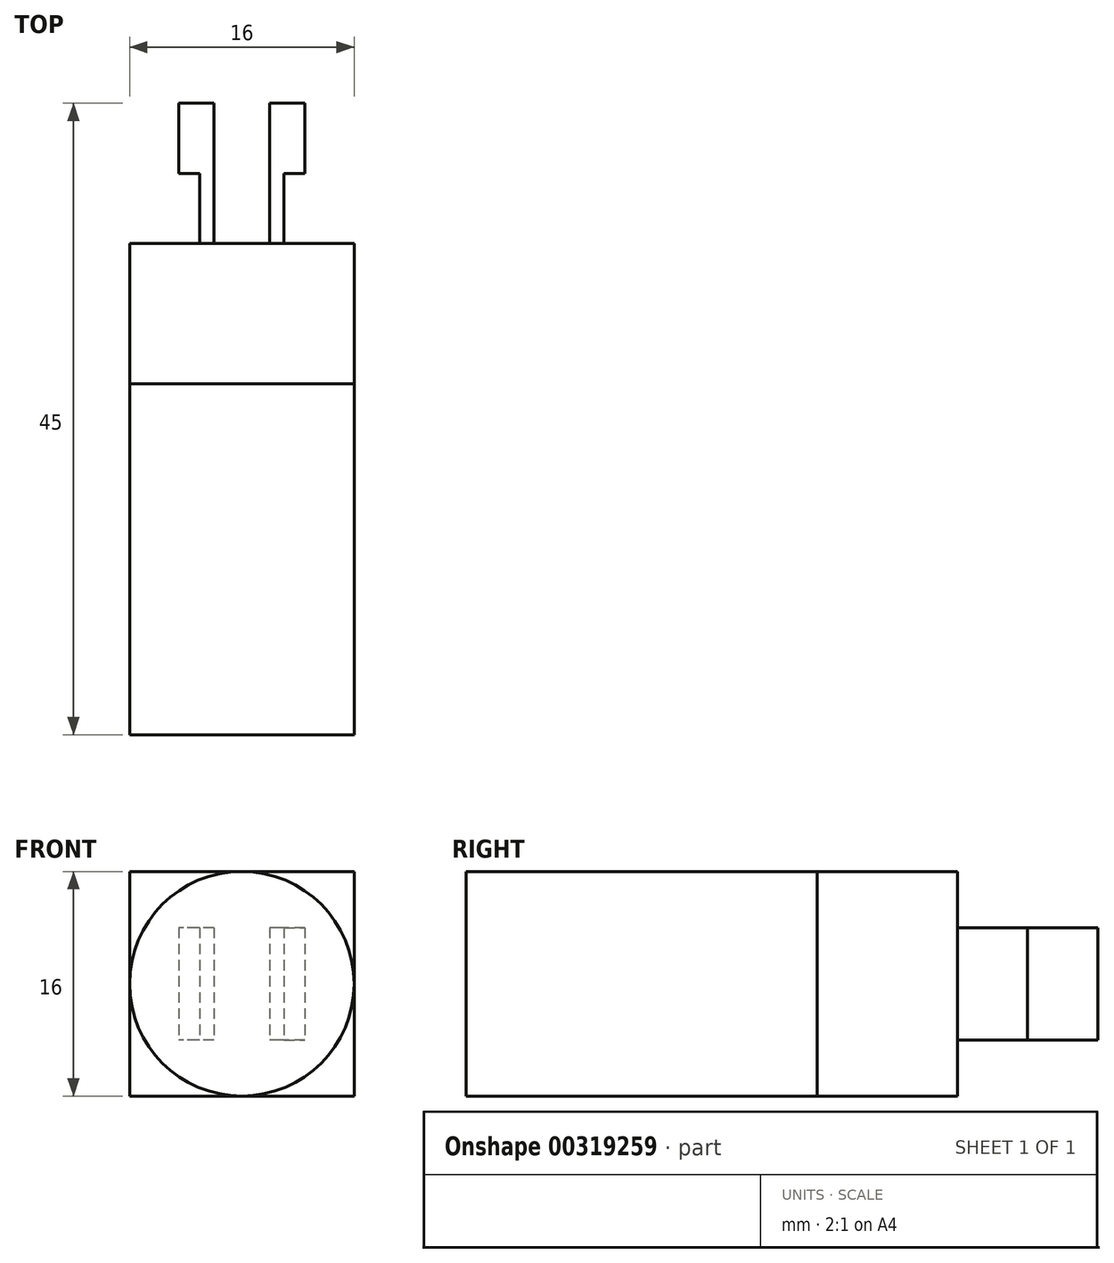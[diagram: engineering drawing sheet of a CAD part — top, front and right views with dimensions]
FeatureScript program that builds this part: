
annotation { "Feature Type Name" : "Feature", "Feature Type Description" : "" }
export const myFeature = defineFeature(function(context is Context, id is Id, definition is map)
    precondition{}
    {
        {
            var Q0;
            Q0=qCreatedBy(makeId("Front.planeOp"),FACE);
            var sketch = newSketch(context, id + "F0", { "sketchPlane" : qUnion([Q0])});
            skCircle(sketch, "E0", {"center": v(0, 0) * mm, "radius": 8 * mm});
            skSolve(sketch);
        }
        {
            var Q0;
            Q0 = qSketchRegion(id + "F0", true);
            extrude(context, id + "F1", {"entities" : qUnion([Q0]), "depth" : 25 * mm});
        }
        {
            var Q0;
            Q0=makeQuery(id+"F0.imprint","IMPRINT",FACE,{"disambiguationData":[TD([[makeQuery(id+"F0.imprint","IMPRINT",EDGE,{"derivedFrom":sQuery(id+"F0.wireOp",EDGE,"E0")}),1.0]])]});
            var sketch = newSketch(context, id + "F2", { "sketchPlane" : qUnion([Q0])});
            skLineSegment(sketch, "E1.bottom", {"start": v(-8, 8) * mm, "end": v(8, 8) * mm});
            skLineSegment(sketch, "E1.top", {"start": v(-8, -8) * mm, "end": v(8, -8) * mm});
            skLineSegment(sketch, "E1.left", {"start": v(-8, 8) * mm, "end": v(-8, -8) * mm});
            skLineSegment(sketch, "E1.right", {"start": v(8, 8) * mm, "end": v(8, -8) * mm});
            skPoint(sketch, "E1.middle", {"position": v(0, 0) * mm});
            skSolve(sketch);
        }
        {
            var Q0;
            Q0 = qSketchRegion(id + "F2", true);
            extrude(context, id + "F3", {"entities" : qUnion([Q0]), "operationType" : NewBodyOperationType.ADD, "oppositeDirection" : true, "depth" : 10 * mm});
        }
        {
            var Q0;
            Q0=makeQuery(id+"F3.opExtrude","CAP_FACE",FACE,{"disambiguationData":[OSD([sQuery(id+"F2.wireOp",EDGE,"E1.bottom"),sQuery(id+"F2.wireOp",EDGE,"E1.top"),sQuery(id+"F2.wireOp",EDGE,"E1.left"),sQuery(id+"F2.wireOp",EDGE,"E1.right")])],"isStart":false});
            var sketch = newSketch(context, id + "F4", { "sketchPlane" : qUnion([Q0])});
            skLineSegment(sketch, "E2.bottom", {"start": v(2, 4) * mm, "end": v(3, 4) * mm});
            skLineSegment(sketch, "E2.top", {"start": v(2, -4) * mm, "end": v(3, -4) * mm});
            skLineSegment(sketch, "E2.left", {"start": v(2, 4) * mm, "end": v(2, -4) * mm});
            skLineSegment(sketch, "E2.right", {"start": v(3, 4) * mm, "end": v(3, -4) * mm});
            skPoint(sketch, "E2.middle", {"position": v(2.5, 0) * mm});
            skLineSegment(sketch, "E3.bottom", {"start": v(-3, 4) * mm, "end": v(-2, 4) * mm});
            skLineSegment(sketch, "E3.top", {"start": v(-3, -4) * mm, "end": v(-2, -4) * mm});
            skLineSegment(sketch, "E3.left", {"start": v(-3, 4) * mm, "end": v(-3, -4) * mm});
            skLineSegment(sketch, "E3.right", {"start": v(-2, 4) * mm, "end": v(-2, -4) * mm});
            skPoint(sketch, "E3.middle", {"position": v(-2.5, 0) * mm});
            skSolve(sketch);
        }
        {
            var Q0;
            Q0 = qSketchRegion(id + "F4", true);
            extrude(context, id + "F5", {"entities" : qUnion([Q0]), "operationType" : NewBodyOperationType.ADD, "depth" : 10 * mm});
        }
        {
            var Q0;
            Q0=makeQuery(id+"F5.opExtrude","CAP_FACE",FACE,{"disambiguationData":[OSD([sQuery(id+"F4.wireOp",EDGE,"E2.bottom"),sQuery(id+"F4.wireOp",EDGE,"E2.top"),sQuery(id+"F4.wireOp",EDGE,"E2.left"),sQuery(id+"F4.wireOp",EDGE,"E2.right")])],"isStart":false});
            var sketch = newSketch(context, id + "F6", { "sketchPlane" : qUnion([Q0])});
            skLineSegment(sketch, "E4.bottom", {"start": v(2, 4) * mm, "end": v(4.5, 4) * mm});
            skLineSegment(sketch, "E4.top", {"start": v(2, -4) * mm, "end": v(4.5, -4) * mm});
            skLineSegment(sketch, "E4.left", {"start": v(2, 4) * mm, "end": v(2, -4) * mm});
            skLineSegment(sketch, "E4.right", {"start": v(4.5, 4) * mm, "end": v(4.5, -4) * mm});
            skPoint(sketch, "E4.middle", {"position": v(3.25, 0) * mm});
            skLineSegment(sketch, "E5.bottom", {"start": v(-2, 4) * mm, "end": v(-4.5, 4) * mm});
            skLineSegment(sketch, "E5.top", {"start": v(-2, -4) * mm, "end": v(-4.5, -4) * mm});
            skLineSegment(sketch, "E5.left", {"start": v(-2, 4) * mm, "end": v(-2, -4) * mm});
            skLineSegment(sketch, "E5.right", {"start": v(-4.5, 4) * mm, "end": v(-4.5, -4) * mm});
            skPoint(sketch, "E5.middle", {"position": v(-3.25, 0) * mm});
            skSolve(sketch);
        }
        {
            var Q0;
            Q0 = qSketchRegion(id + "F6", true);
            extrude(context, id + "F7", {"entities" : qUnion([Q0]), "operationType" : NewBodyOperationType.ADD, "oppositeDirection" : true, "depth" : 5 * mm});
        }
    });
